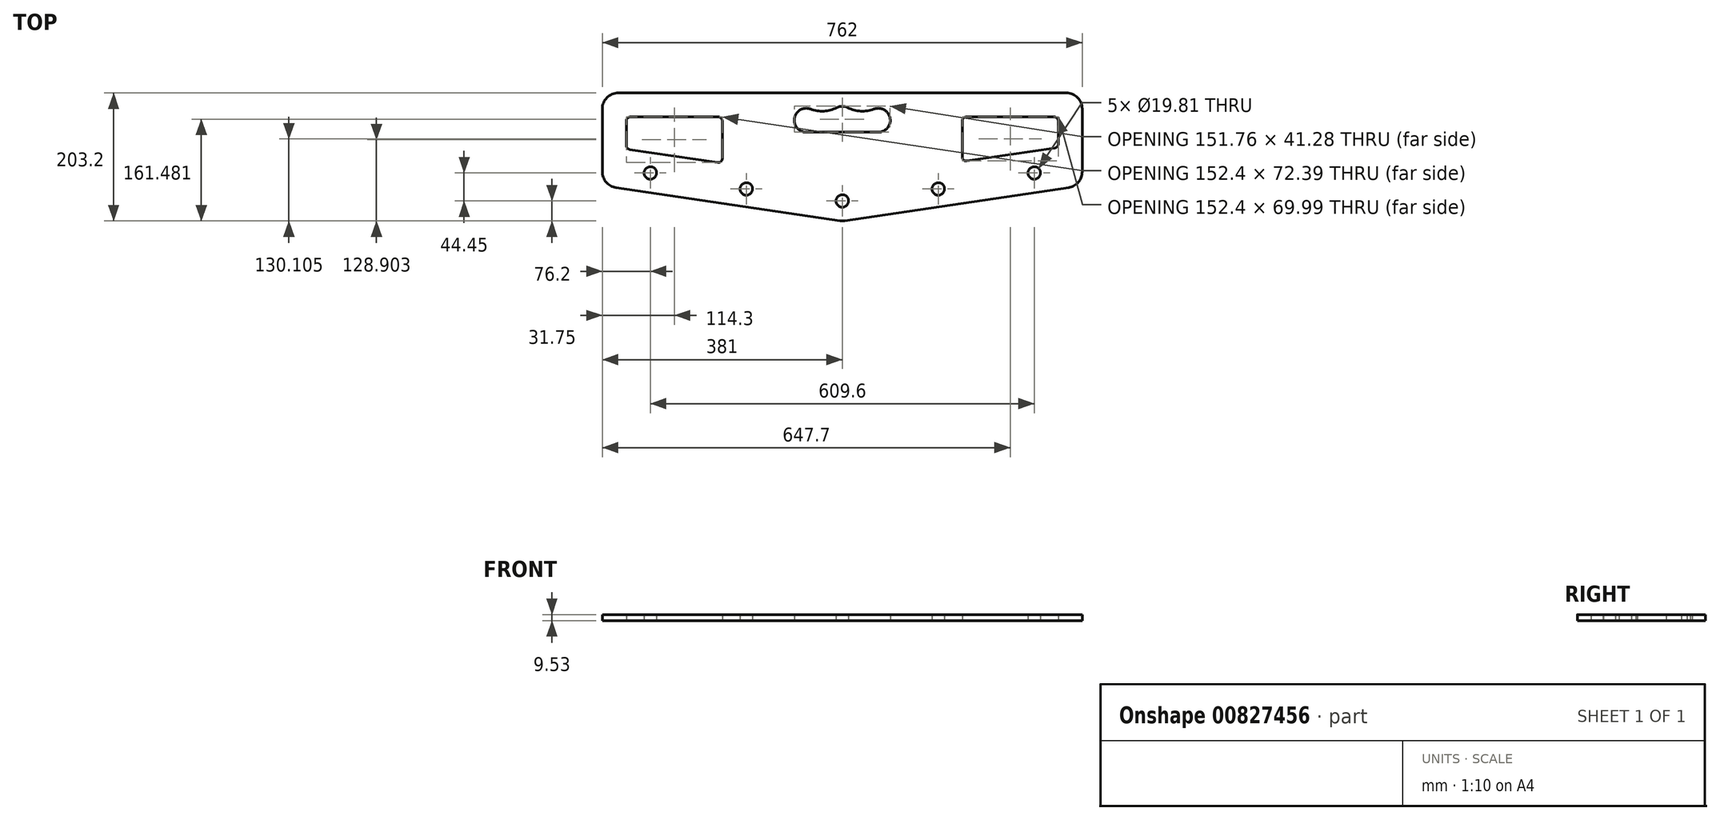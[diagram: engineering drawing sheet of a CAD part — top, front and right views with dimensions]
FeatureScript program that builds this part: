
annotation { "Feature Type Name" : "Feature", "Feature Type Description" : "" }
export const myFeature = defineFeature(function(context is Context, id is Id, definition is map)
    precondition{}
    {
        {
            var Q0;
            Q0=qCreatedBy(makeId("Top.planeOp"),FACE);
            var sketch = newSketch(context, id + "F0", { "sketchPlane" : qUnion([Q0])});
            skLineSegment(sketch, "E0.top", {"start": v(25.4, 203.2) * mm, "end": v(736.6, 203.2) * mm});
            skLineSegment(sketch, "E0.left", {"start": v(0, 78.18) * mm, "end": v(0, 177.8) * mm});
            skLineSegment(sketch, "E0.right", {"start": v(762, 78.18) * mm, "end": v(762, 177.8) * mm});
            skLineSegment(sketch, "E1.top", {"start": v(44.45, 165.1) * mm, "end": v(184.15, 165.1) * mm});
            skLineSegment(sketch, "E1.left", {"start": v(38.1, 119.78) * mm, "end": v(38.1, 158.75) * mm});
            skLineSegment(sketch, "E1.right", {"start": v(190.5, 99.04) * mm, "end": v(190.5, 158.75) * mm});
            skLineSegment(sketch, "E2.top", {"start": v(577.85, 165.1) * mm, "end": v(717.55, 165.1) * mm});
            skLineSegment(sketch, "E2.left", {"start": v(571.5, 101.45) * mm, "end": v(571.5, 158.75) * mm});
            skLineSegment(sketch, "E2.right", {"start": v(723.9, 122.18) * mm, "end": v(723.9, 158.75) * mm});
            skCircle(sketch, "E3", {"center": v(381, 31.75) * mm, "radius": 9.9 * mm});
            skArc(sketch, "E4", {"start": v(377.27, 0.28) * mm, "mid": v(381, 0) * mm, "end": v(384.73, 0.28) * mm});
            skLineSegment(sketch, "E5", {"start": v(21.67, 53.05) * mm, "end": v(377.27, 0.28) * mm});
            skLineSegment(sketch, "E6", {"start": v(740.33, 53.05) * mm, "end": v(384.73, 0.28) * mm});
            skPoint(sketch, "E7.visualSharp", {"position": v(38.1, 165.1) * mm});
            skArc(sketch, "E7.filletArc", {"start": v(44.45, 165.1) * mm, "mid": v(39.96, 163.24) * mm, "end": v(38.1, 158.75) * mm});
            skPoint(sketch, "E8.visualSharp", {"position": v(38.1, 114.3) * mm});
            skPoint(sketch, "E9.visualSharp", {"position": v(190.5, 114.3) * mm});
            skPoint(sketch, "E10.visualSharp", {"position": v(190.5, 165.1) * mm});
            skArc(sketch, "E10.filletArc", {"start": v(190.5, 158.75) * mm, "mid": v(188.64, 163.24) * mm, "end": v(184.15, 165.1) * mm});
            skPoint(sketch, "E11.visualSharp", {"position": v(571.5, 165.1) * mm});
            skArc(sketch, "E11.filletArc", {"start": v(577.85, 165.1) * mm, "mid": v(573.36, 163.24) * mm, "end": v(571.5, 158.75) * mm});
            skPoint(sketch, "E12.visualSharp", {"position": v(571.5, 114.3) * mm});
            skPoint(sketch, "E13.visualSharp", {"position": v(723.9, 165.1) * mm});
            skArc(sketch, "E13.filletArc", {"start": v(723.9, 158.75) * mm, "mid": v(722.04, 163.24) * mm, "end": v(717.55, 165.1) * mm});
            skPoint(sketch, "E14.visualSharp", {"position": v(723.9, 116.7) * mm});
            skPoint(sketch, "E15.visualSharp", {"position": v(762, 203.2) * mm});
            skArc(sketch, "E15.filletArc", {"start": v(762, 177.8) * mm, "mid": v(754.56, 195.76) * mm, "end": v(736.6, 203.2) * mm});
            skPoint(sketch, "E16.visualSharp", {"position": v(0, 203.2) * mm});
            skArc(sketch, "E16.filletArc", {"start": v(25.4, 203.2) * mm, "mid": v(7.44, 195.76) * mm, "end": v(0, 177.8) * mm});
            skPoint(sketch, "E17.newPointA", {"position": v(0, 0) * mm});
            skPoint(sketch, "E17.newPointB", {"position": v(74.89, 45.16) * mm});
            skArc(sketch, "E17.filletArc", {"start": v(0, 78.18) * mm, "mid": v(6.17, 61.59) * mm, "end": v(21.67, 53.05) * mm});
            skPoint(sketch, "E18.newPointB", {"position": v(611.86, 33.99) * mm});
            skArc(sketch, "E18.filletArc", {"start": v(740.33, 53.05) * mm, "mid": v(755.83, 61.59) * mm, "end": v(762, 78.18) * mm});
            skLineSegment(sketch, "E19.bottom", {"start": v(323.85, 140.84) * mm, "end": v(438.15, 140.84) * mm});
            skArc(sketch, "E20", {"start": v(391.53, 178.94) * mm, "mid": v(381, 182.12) * mm, "end": v(370.47, 178.94) * mm});
            skPoint(sketch, "E20.centerSnap0", {"position": v(381, 178.94) * mm});
            skArc(sketch, "E21", {"start": v(330.68, 177.68) * mm, "mid": v(305.12, 163.37) * mm, "end": v(323.85, 140.84) * mm});
            skPoint(sketch, "E21.centerSnap0", {"position": v(304.8, 159.9) * mm});
            skArc(sketch, "E22", {"start": v(438.15, 140.84) * mm, "mid": v(456.88, 163.37) * mm, "end": v(431.32, 177.68) * mm});
            skPoint(sketch, "E23.orphan", {"position": v(323.85, 178.94) * mm});
            skArc(sketch, "E24", {"start": v(389.76, 179.99) * mm, "mid": v(410.3, 174.38) * mm, "end": v(431.32, 177.68) * mm});
            skArc(sketch, "E25.trimOffspring", {"start": v(330.68, 177.68) * mm, "mid": v(351.7, 174.38) * mm, "end": v(372.24, 179.99) * mm});
            skPoint(sketch, "E26", {"position": v(381, 0) * mm});
            skLineSegment(sketch, "E27", {"start": v(43.52, 113.5) * mm, "end": v(183.22, 92.76) * mm});
            skLineSegment(sketch, "E28", {"start": v(718.48, 115.9) * mm, "end": v(578.78, 95.16) * mm});
            skPoint(sketch, "E29.visualSharp", {"position": v(190.5, 91.68) * mm});
            skArc(sketch, "E29.filletArc", {"start": v(183.22, 92.76) * mm, "mid": v(188.3, 94.23) * mm, "end": v(190.5, 99.04) * mm});
            skArc(sketch, "E30.filletArc", {"start": v(38.1, 119.78) * mm, "mid": v(39.64, 115.63) * mm, "end": v(43.52, 113.5) * mm});
            skPoint(sketch, "E31.visualSharp", {"position": v(571.5, 94.08) * mm});
            skArc(sketch, "E31.filletArc", {"start": v(571.5, 101.45) * mm, "mid": v(573.7, 96.64) * mm, "end": v(578.78, 95.16) * mm});
            skArc(sketch, "E32.filletArc", {"start": v(718.48, 115.9) * mm, "mid": v(722.36, 118.03) * mm, "end": v(723.9, 122.18) * mm});
            skCircle(sketch, "E33", {"center": v(228.6, 50.8) * mm, "radius": 9.9 * mm});
            skCircle(sketch, "E34", {"center": v(533.4, 50.8) * mm, "radius": 9.9 * mm});
            skPoint(sketch, "E35", {"position": v(762, 53.05) * mm});
            skCircle(sketch, "E36", {"center": v(76.2, 76.2) * mm, "radius": 9.9 * mm});
            skCircle(sketch, "E37", {"center": v(685.8, 76.2) * mm, "radius": 9.9 * mm});
            skSolve(sketch);
        }
        {
            var Q0;
            Q0=makeQuery(id+"F0.imprint","IMPRINT",FACE,{"disambiguationData":[TD([[makeQuery(id+"F0.imprint","IMPRINT",EDGE,{"derivedFrom":sQuery(id+"F0.wireOp",EDGE,"E0.top")}),-1.0]])]});
            extrude(context, id + "F1", {"entities" : qUnion([Q0]), "depth" : 9.52 * mm, "offsetDistance" : 25.4 * mm});
        }
    });
